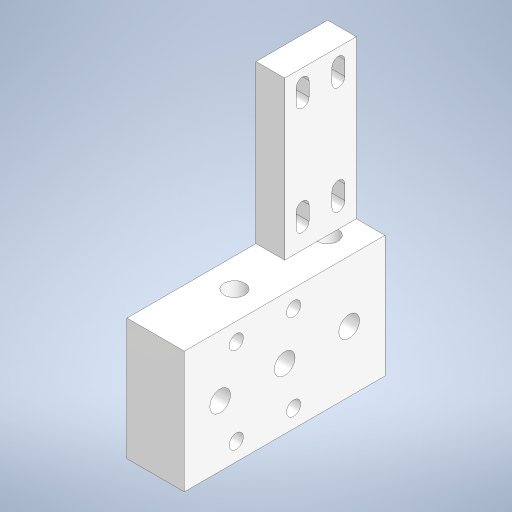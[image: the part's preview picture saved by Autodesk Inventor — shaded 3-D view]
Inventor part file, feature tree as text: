
AUTODESK INVENTOR PART (.ipt)
format: ipt  version: 2024.1 (Build 281209000, 209)  size: 381,440 bytes
history: native  units: in
note: dims shown in document units (in); Inventor stores cm internally (conversion verified against a paired STEP export)
features: extrude x7, sketch x7, chamfer x2, mirror x1
ambient origin geometry x8: Origin, YZ Plane, XZ Plane, XY Plane, X Axis, Y Axis, Z Axis, Center Point
bodies: Solid1 (feature_tree)
feature tree (17):
  extrude  "Extrusion1"  Depth=1.1024in
  extrude  "Extrusion2"  Depth=0.3937in
  extrude  "Extrusion3"  Depth=0.315in TaperAngle=0.0deg
  extrude  "Extrusion4"  TaperAngle=0.0deg  [1 undecoded]
  extrude  "Extrusion5"  Depth=0.0787in
  chamfer  "Chamfer1"  Distance=0.0984in
  extrude  "Extrusion7"  Depth=0.0354in
  chamfer  "Chamfer3"  Distance=0.0984in
  extrude  "Extrusion8"  Depth=0.0354in
  mirror  "Mirror1"
  sketch  "Sketch1"  dims[d0=0.6693in d1=1.1024in]
  sketch  "Sketch2"  dims[d2=0.315in d3=0.0in d4=0.3937in]
  sketch  "Sketch3"  dims[d5=0.8661in d6=0.315in d7=0.0in]
  sketch  "Sketch4"  dims[d8=0.1575in d9=0.0in d10=0.0in]
  sketch  "Sketch5"  dims[d11=0.0787in d13=0.0787in]
  sketch  "Sketch8"  dims[d14=0.0787in]
  sketch  "Sketch9"  dims[d15=0.0787in d16=0.0984in d17=0.0984in d18=0.0984in d19=0.0984in d20=0.2854in d21=0.2854in d22=0.315in d23=0.315in d24=0.0in d25=0.0in d26=0.1142in d27=0.1142in d28=0.1575in d29=0.1575in d30=0.6693in d31=0.0in d32=0.0in d33=0.0079in d34=0.0787in d35=45.0deg d53=0.3346in d54=0.3346in d55=0.3346in d56=0.1142in d57=0.1142in d58=0.1142in d59=0.1969in d60=0.5512in d61=0.1969in d62=0.0in d63=0.0in d64=0.0551in d65=0.0787in d66=45.0deg d70=0.0709in d71=0.0709in d72=0.0709in d73=0.0709in d74=0.0984in d75=0.0787in d76=0.0787in d77=0.0984in d78=0.0984in d79=0.0984in d80=0.5906in d81=0.5906in d82=0.0709in d83=0.0709in d84=0.0709in d85=0.0787in d86=0.0787in d87=0.0787in d88=0.0354in d89=0.0354in d90=0.0in d91=0.0in]
note: 1 required parameter value undecoded (feature->parameter linkage not recoverable at this tier; creation-order binding heuristic only, values carry confidence <= 0.55)
